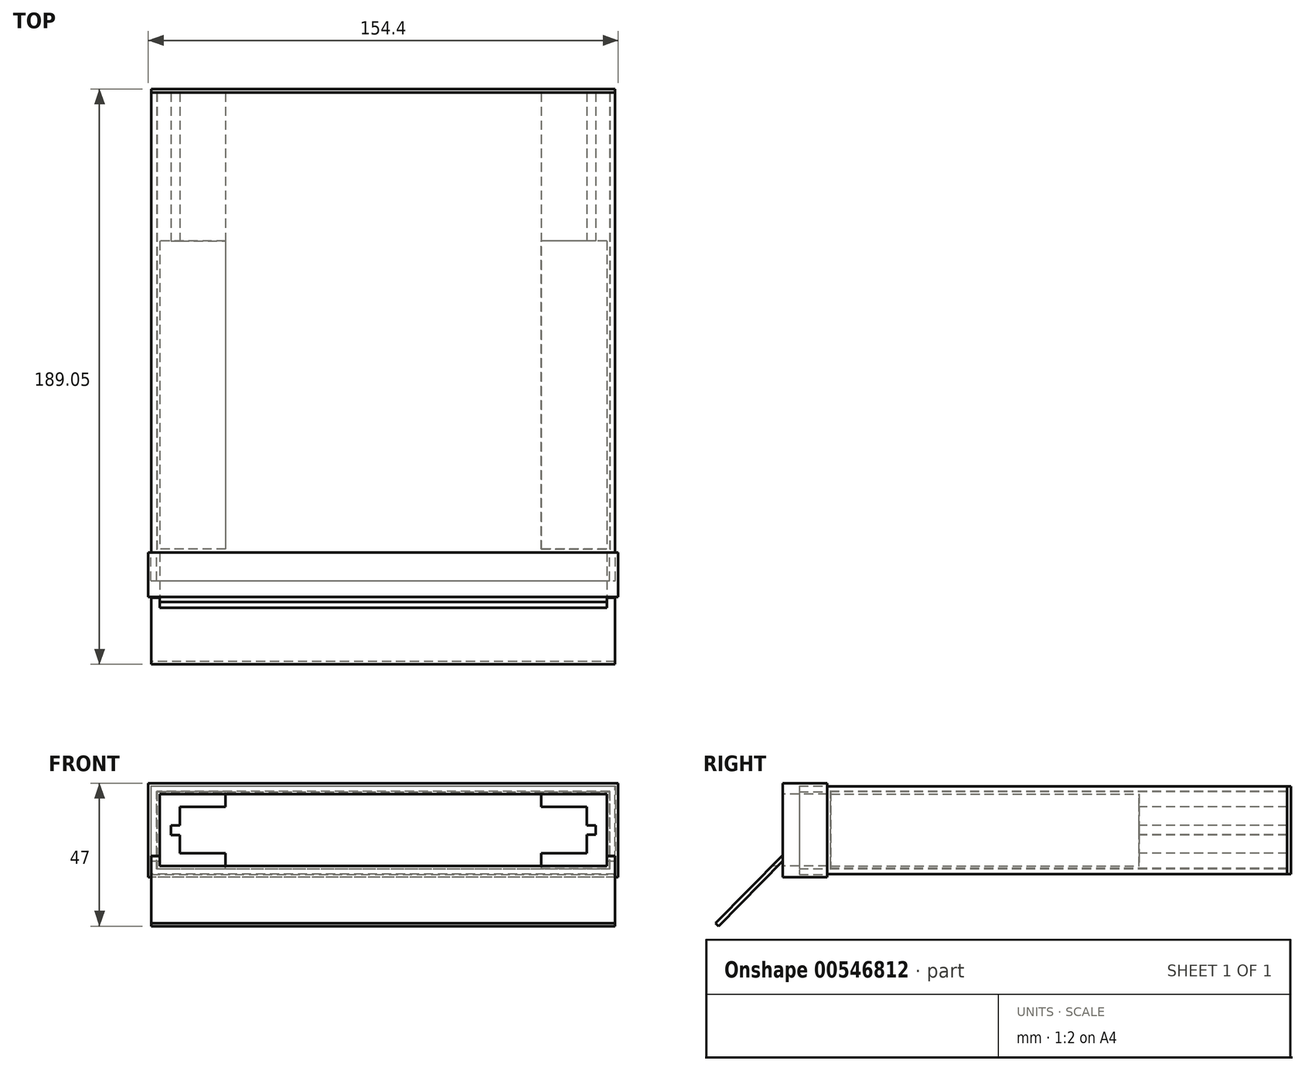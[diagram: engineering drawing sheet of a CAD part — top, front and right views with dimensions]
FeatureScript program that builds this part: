
annotation { "Feature Type Name" : "Feature", "Feature Type Description" : "" }
export const myFeature = defineFeature(function(context is Context, id is Id, definition is map)
    precondition{}
    {
        {
            var Q0;
            Q0=qCreatedBy(makeId("Front.planeOp"),FACE);
            var sketch = newSketch(context, id + "F0", { "sketchPlane" : qUnion([Q0])});
            skLineSegment(sketch, "E0.bottom", {"start": v(74.5, -12.75) * mm, "end": v(-74.5, -12.75) * mm});
            skLineSegment(sketch, "E0.top", {"start": v(74.5, 12.75) * mm, "end": v(-74.5, 12.75) * mm});
            skLineSegment(sketch, "E0.left", {"start": v(74.5, -12.75) * mm, "end": v(74.5, 12.75) * mm});
            skLineSegment(sketch, "E0.right", {"start": v(-74.5, -12.75) * mm, "end": v(-74.5, 12.75) * mm});
            skPoint(sketch, "E0.middle", {"position": v(0, 0) * mm});
            skLineSegment(sketch, "E1.0", {"start": v(-76.2, -14.45) * mm, "end": v(-76.2, 14.45) * mm});
            skLineSegment(sketch, "E1.1", {"start": v(76.2, -14.45) * mm, "end": v(-76.2, -14.45) * mm});
            skLineSegment(sketch, "E1.2", {"start": v(76.2, -14.45) * mm, "end": v(76.2, 14.45) * mm});
            skLineSegment(sketch, "E1.3", {"start": v(76.2, 14.45) * mm, "end": v(-76.2, 14.45) * mm});
            skSolve(sketch);
        }
        {
            var Q0;
            Q0 = qSketchRegion(id + "F0", true);
            extrude(context, id + "F1", {"entities" : qUnion([Q0]), "oppositeDirection" : true, "depth" : 160 * mm, "offsetDistance" : 25 * mm});
        }
        {
            var Q0;
            Q0=qCreatedBy(makeId("Front.planeOp"),FACE);
            var sketch = newSketch(context, id + "F2", { "sketchPlane" : qUnion([Q0])});
            skLineSegment(sketch, "E2", {"start": v(-74.3, 12.6) * mm, "end": v(-74.3, -12.6) * mm});
            skLineSegment(sketch, "E3", {"start": v(-74.3, -12.6) * mm, "end": v(-51.8, -12.6) * mm});
            skLineSegment(sketch, "E4", {"start": v(-51.8, -12.6) * mm, "end": v(-51.8, -7.6) * mm});
            skLineSegment(sketch, "E5", {"start": v(-51.8, -7.6) * mm, "end": v(-66.8, -7.6) * mm});
            skLineSegment(sketch, "E6", {"start": v(-66.8, -7.6) * mm, "end": v(-66.8, -1.55) * mm});
            skLineSegment(sketch, "E7", {"start": v(-66.8, -1.55) * mm, "end": v(-69.8, -1.55) * mm});
            skLineSegment(sketch, "E8", {"start": v(-69.8, -1.55) * mm, "end": v(-69.8, 1.54) * mm});
            skLineSegment(sketch, "E9", {"start": v(-69.8, 1.54) * mm, "end": v(-66.8, 1.54) * mm});
            skLineSegment(sketch, "E10", {"start": v(-66.8, 1.54) * mm, "end": v(-66.8, 7.6) * mm});
            skLineSegment(sketch, "E11", {"start": v(-66.8, 7.6) * mm, "end": v(-51.8, 7.6) * mm});
            skLineSegment(sketch, "E12", {"start": v(-51.8, 7.6) * mm, "end": v(-51.8, 12.6) * mm});
            skLineSegment(sketch, "E13", {"start": v(-51.8, 12.6) * mm, "end": v(-74.3, 12.6) * mm});
            skSolve(sketch);
        }
        {
            var Q0;
            Q0=makeQuery(id+"F2.imprint","IMPRINT",FACE,{"disambiguationData":[TD([[makeQuery(id+"F2.imprint","IMPRINT",EDGE,{"derivedFrom":sQuery(id+"F2.wireOp",EDGE,"E2")}),1.0]])]});
            extrude(context, id + "F3", {"entities" : qUnion([Q0]), "oppositeDirection" : true, "depth" : 160 * mm, "hasOffset" : true, "offsetDistance" : 20 * mm, "hasSecondDirection" : true, "secondDirectionOppositeDirection" : true, "secondDirectionDepth" : 10 * mm});
        }
        {
            var Q0;
            Q0=qCreatedBy(makeId("Front.planeOp"),FACE);
            var sketch = newSketch(context, id + "F4", { "sketchPlane" : qUnion([Q0])});
            skLineSegment(sketch, "E14", {"start": v(51.88, 12.6) * mm, "end": v(51.88, 7.6) * mm});
            skLineSegment(sketch, "E15", {"start": v(51.88, 7.6) * mm, "end": v(66.88, 7.6) * mm});
            skLineSegment(sketch, "E16", {"start": v(66.88, 7.6) * mm, "end": v(66.88, 1.55) * mm});
            skLineSegment(sketch, "E17", {"start": v(66.88, 1.55) * mm, "end": v(69.88, 1.55) * mm});
            skLineSegment(sketch, "E18", {"start": v(69.88, 1.55) * mm, "end": v(69.88, -1.55) * mm});
            skLineSegment(sketch, "E19", {"start": v(69.88, -1.55) * mm, "end": v(66.88, -1.55) * mm});
            skLineSegment(sketch, "E20", {"start": v(66.88, -1.55) * mm, "end": v(66.88, -7.6) * mm});
            skLineSegment(sketch, "E21", {"start": v(66.88, -7.6) * mm, "end": v(51.88, -7.6) * mm});
            skLineSegment(sketch, "E22", {"start": v(51.88, -7.6) * mm, "end": v(51.88, -12.6) * mm});
            skLineSegment(sketch, "E23", {"start": v(51.88, -12.6) * mm, "end": v(74.38, -12.6) * mm});
            skLineSegment(sketch, "E24", {"start": v(74.38, -12.6) * mm, "end": v(74.38, 12.6) * mm});
            skLineSegment(sketch, "E25", {"start": v(74.38, 12.6) * mm, "end": v(51.88, 12.6) * mm});
            skSolve(sketch);
        }
        {
            var Q0;
            Q0=makeQuery(id+"F4.imprint","IMPRINT",FACE,{"disambiguationData":[TD([[makeQuery(id+"F4.imprint","IMPRINT",EDGE,{"derivedFrom":sQuery(id+"F4.wireOp",EDGE,"E14")}),1.0]])]});
            extrude(context, id + "F5", {"entities" : qUnion([Q0]), "oppositeDirection" : true, "depth" : 160 * mm, "offsetDistance" : 25 * mm, "hasSecondDirection" : true, "secondDirectionOppositeDirection" : true, "secondDirectionDepth" : 10 * mm});
        }
        {
            var Q0;
            Q0=qCreatedBy(makeId("Right.planeOp"),FACE);
            var sketch = newSketch(context, id + "F6", { "sketchPlane" : qUnion([Q0])});
            skLineSegment(sketch, "E26.bottom", {"start": v(161.2, -14.44) * mm, "end": v(160, -14.44) * mm});
            skLineSegment(sketch, "E26.top", {"start": v(161.2, 14.44) * mm, "end": v(160, 14.44) * mm});
            skLineSegment(sketch, "E26.left", {"start": v(161.2, -14.44) * mm, "end": v(161.2, 14.44) * mm});
            skLineSegment(sketch, "E26.right", {"start": v(160, -14.44) * mm, "end": v(160, 14.44) * mm});
            skPoint(sketch, "E26.middle", {"position": v(160.6, 0) * mm});
            skSolve(sketch);
        }
        {
            var Q0;
            Q0 = qSketchRegion(id + "F6", true);
            extrude(context, id + "F7", {"entities" : qUnion([Q0]), "endBound" : BoundingType.SYMMETRIC, "depth" : 152.4 * mm, "offsetDistance" : 25 * mm});
        }
        {
            var Q0;
            Q0=qCreatedBy(makeId("Right.planeOp"),FACE);
            var sketch = newSketch(context, id + "F8", { "sketchPlane" : qUnion([Q0])});
            skLineSegment(sketch, "E27", {"start": v(-5, -9.44) * mm, "end": v(-26.85, -31.54) * mm});
            skLineSegment(sketch, "E28", {"start": v(-27.85, -30.55) * mm, "end": v(-26.85, -31.54) * mm});
            skLineSegment(sketch, "E29", {"start": v(-27.85, -30.55) * mm, "end": v(-6, -8.46) * mm});
            skLineSegment(sketch, "E30", {"start": v(-5, -9.44) * mm, "end": v(-6, -8.46) * mm});
            skSolve(sketch);
        }
        {
            var Q0;
            Q0 = qSketchRegion(id + "F8", true);
            extrude(context, id + "F9", {"entities" : qUnion([Q0]), "endBound" : BoundingType.SYMMETRIC, "depth" : 152.4 * mm, "offsetDistance" : 25 * mm});
        }
        {
            var Q0;
            Q0=qCreatedBy(makeId("Right.planeOp"),FACE);
            var sketch = newSketch(context, id + "F10", { "sketchPlane" : qUnion([Q0])});
            skLineSegment(sketch, "E31.bottom", {"start": v(-1.12, 15.46) * mm, "end": v(8.88, 15.46) * mm});
            skLineSegment(sketch, "E31.top", {"start": v(-1.12, -15.46) * mm, "end": v(8.88, -15.46) * mm});
            skLineSegment(sketch, "E31.left", {"start": v(-1.12, 15.46) * mm, "end": v(-1.12, -15.46) * mm});
            skLineSegment(sketch, "E31.right", {"start": v(8.88, 15.46) * mm, "end": v(8.88, -15.46) * mm});
            skPoint(sketch, "E31.middle", {"position": v(3.88, 0) * mm});
            skSolve(sketch);
        }
        {
            var Q0;
            Q0 = qSketchRegion(id + "F10", true);
            extrude(context, id + "F11", {"entities" : qUnion([Q0]), "endBound" : BoundingType.SYMMETRIC, "depth" : 154.4 * mm, "offsetDistance" : 25 * mm});
        }
        {
            var Q0;
            Q0=makeQuery(id+"F11.opExtrude","SWEPT_FACE",FACE,{"disambiguationData":[OSD([sQuery(id+"F10.wireOp",EDGE,"E31.left")])]});
            var sketch = newSketch(context, id + "F12", { "sketchPlane" : qUnion([Q0])});
            skLineSegment(sketch, "E32.bottom", {"start": v(73.45, -11.79) * mm, "end": v(-73.45, -11.79) * mm});
            skLineSegment(sketch, "E32.top", {"start": v(73.45, 11.79) * mm, "end": v(-73.45, 11.79) * mm});
            skLineSegment(sketch, "E32.left", {"start": v(73.45, -11.79) * mm, "end": v(73.45, 11.79) * mm});
            skLineSegment(sketch, "E32.right", {"start": v(-73.45, -11.79) * mm, "end": v(-73.45, 11.79) * mm});
            skPoint(sketch, "E32.middle", {"position": v(0, 0) * mm});
            skSolve(sketch);
        }
        {
            var Q0;
            Q0 = qSketchRegion(id + "F12", true);
            extrude(context, id + "F13", {"entities" : qUnion([Q0]), "operationType" : NewBodyOperationType.REMOVE, "endBound" : BoundingType.SYMMETRIC, "oppositeDirection" : true, "depth" : 224.8 * mm, "offsetDistance" : 25 * mm});
        }
        {
            var Q0;
            Q0=makeQuery(id+"F11.opExtrude","SWEPT_FACE",FACE,{"disambiguationData":[OSD([sQuery(id+"F10.wireOp",EDGE,"E31.right")])]});
            var sketch = newSketch(context, id + "F14", { "sketchPlane" : qUnion([Q0])});
            skLineSegment(sketch, "E33.bottom", {"start": v(74.41, 12.66) * mm, "end": v(-74.41, 12.66) * mm});
            skLineSegment(sketch, "E33.top", {"start": v(74.41, -12.66) * mm, "end": v(-74.41, -12.66) * mm});
            skLineSegment(sketch, "E33.left", {"start": v(-74.41, 12.66) * mm, "end": v(-74.41, -12.66) * mm});
            skLineSegment(sketch, "E33.right", {"start": v(74.41, 12.66) * mm, "end": v(74.41, -12.66) * mm});
            skPoint(sketch, "E33.middle", {"position": v(0, 0) * mm});
            skLineSegment(sketch, "E34.bottom", {"start": v(76.31, 14.54) * mm, "end": v(-76.31, 14.54) * mm});
            skLineSegment(sketch, "E34.top", {"start": v(76.31, -14.54) * mm, "end": v(-76.31, -14.54) * mm});
            skLineSegment(sketch, "E34.left", {"start": v(76.31, 14.54) * mm, "end": v(76.31, -14.54) * mm});
            skLineSegment(sketch, "E34.right", {"start": v(-76.31, 14.54) * mm, "end": v(-76.31, -14.54) * mm});
            skSolve(sketch);
        }
        {
            var Q0;
            Q0=makeQuery(id+"F14.imprint","IMPRINT",FACE,{"disambiguationData":[TD([[makeQuery(id+"F14.imprint","IMPRINT",EDGE,{"derivedFrom":sQuery(id+"F14.wireOp",EDGE,"E33.bottom")}),-1.0]])]});
            extrude(context, id + "F15", {"entities" : qUnion([Q0]), "operationType" : NewBodyOperationType.REMOVE, "oppositeDirection" : true, "depth" : 9.2 * mm, "offsetDistance" : 25 * mm});
        }
        {
            var Q0;
            Q0=makeQuery(id+"F11.opExtrude","SWEPT_FACE",FACE,{"disambiguationData":[OSD([sQuery(id+"F10.wireOp",EDGE,"E31.left")])]});
            extrude(context, id + "F16", {"entities" : qUnion([Q0]), "operationType" : NewBodyOperationType.ADD, "depth" : 4.6 * mm, "offsetDistance" : 25 * mm});
        }
    });
